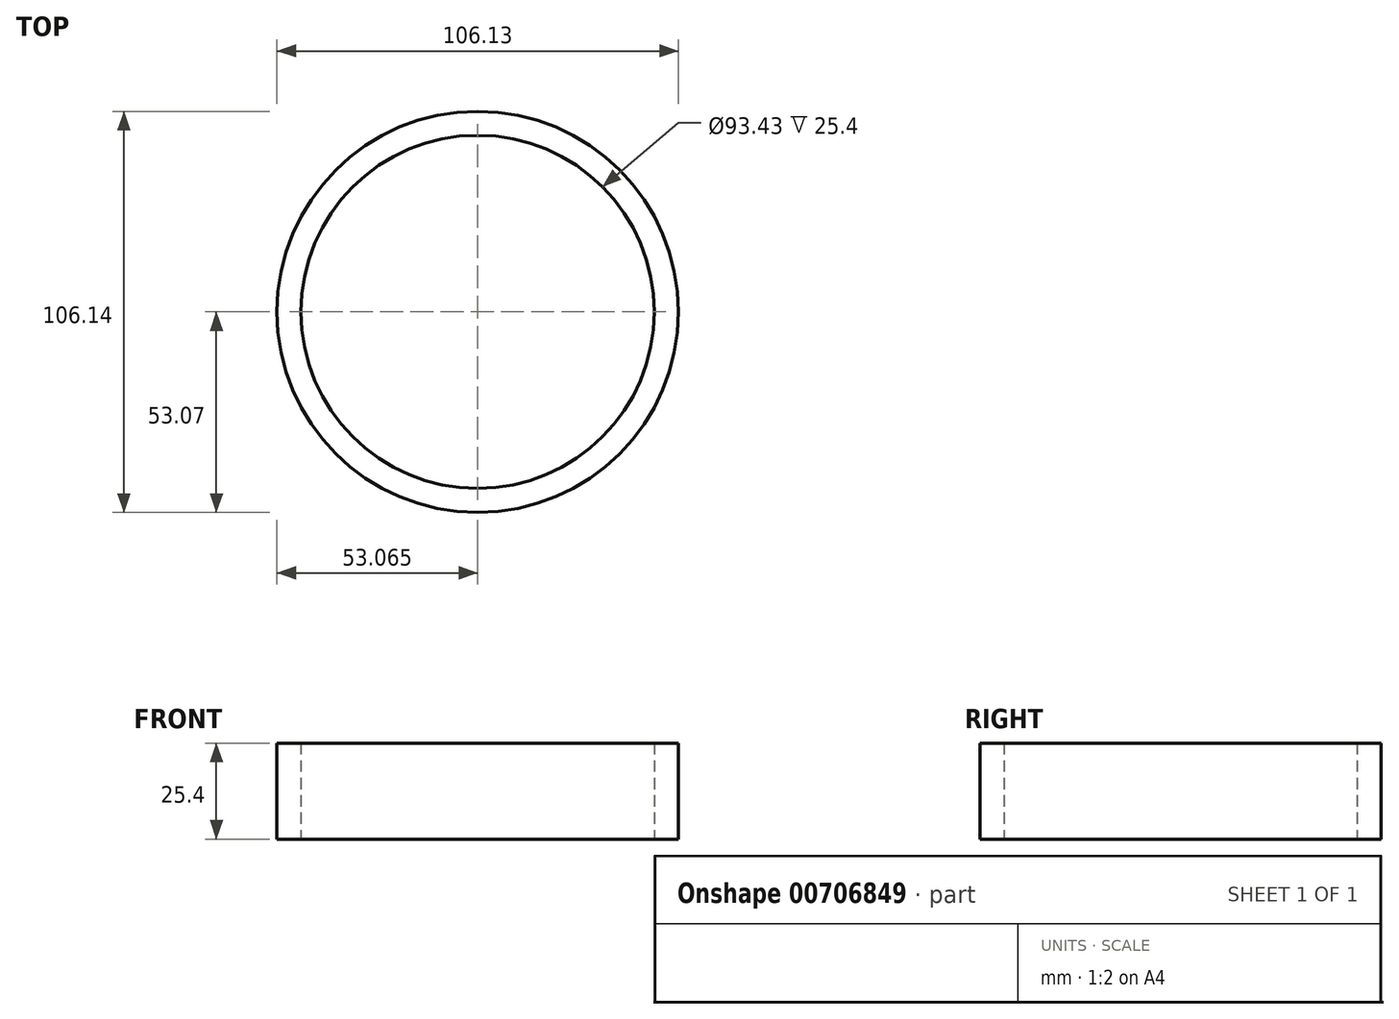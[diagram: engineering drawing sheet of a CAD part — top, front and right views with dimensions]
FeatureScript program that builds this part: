
annotation { "Feature Type Name" : "Feature", "Feature Type Description" : "" }
export const myFeature = defineFeature(function(context is Context, id is Id, definition is map)
    precondition{}
    {
        {
            var Q0;
            Q0=qCreatedBy(makeId("Top.planeOp"),FACE);
            var sketch = newSketch(context, id + "F0", { "sketchPlane" : qUnion([Q0])});
            skCircle(sketch, "E0", {"center": v(-53.85, 0) * mm, "radius": 53.85 * mm});
            skSolve(sketch);
        }
        {
            var Q0;
            Q0=qCreatedBy(makeId("Top.planeOp"),FACE);
            var sketch = newSketch(context, id + "F1", { "sketchPlane" : qUnion([Q0])});
            skCircle(sketch, "E1", {"center": v(-54.51, 0) * mm, "radius": 53.07 * mm});
            skSolve(sketch);
        }
        {
            var Q0;
            Q0=makeQuery(id+"F0.imprint","IMPRINT",FACE,{"disambiguationData":[TD([[makeQuery(id+"F0.imprint","IMPRINT",EDGE,{"derivedFrom":sQuery(id+"F0.wireOp",EDGE,"E0")}),1.0]])]});
            var Q1;
            Q1 = qSketchRegion(id + "F1", true);
            var Q2;
            Q2=makeQuery(id+"F1.imprint","IMPRINT",FACE,{"disambiguationData":[TD([[makeQuery(id+"F1.imprint","IMPRINT",EDGE,{"derivedFrom":sQuery(id+"F1.wireOp",EDGE,"E1")}),1.0]])]});
            extrude(context, id + "F2", {"entities" : qUnion([Q0, Q1, Q2]), "depth" : 25.4 * mm, "offsetDistance" : 25.4 * mm});
        }
        {
            var Q0;
            Q0=makeQuery(id+"F2.opExtrude","SWEPT_BODY",BODY,{"disambiguationData":[OSD([sQuery(id+"F0.wireOp",EDGE,"E0")])]});
            deleteBodies(context, id + "F3", {"entities" : qUnion([Q0])});
        }
        {
            var Q0;
            Q0=makeQuery(id+"F2.opExtrude","CAP_FACE",FACE,{"disambiguationData":[OSD([sQuery(id+"F1.wireOp",EDGE,"E1")])],"isStart":true});
            var Q1;
            Q1=makeQuery(id+"F2.opExtrude","CAP_FACE",FACE,{"disambiguationData":[OSD([sQuery(id+"F1.wireOp",EDGE,"E1")])],"isStart":false});
            shell(context, id + "F4", {"entities" : qUnion([Q0, Q1]), "thickness" : 6.35 * mm});
        }
    });
